# Revit family: TYCO-FPP-Zettler-QRM850 Quad relay output module
name_source: partatom
category: Electrical Fixtures
revit_build: Autodesk Revit 2014 (Build: 20130308_1515(x64)
units: mm (PartAtom-declared; Revit-internal decimal feet)

## types (1)
- TYCO-FPP-Zettler-QRM850 Quad relay output module
    Alarm current = 5.9 mA
    Approvals = EN54-17, EN54-18 and
EN54-13
    Battery Requirements = Standby current
1.1 mA
    Description = The Quad Relay Output Module connects directly to the
MZX Digital loop and provides four change over relay
outputs or four High Voltage Relay (HVR) outputs.
    Keynote = Four change over relay outputs each individually
programmable for a wide range of applications
    Length = 103 mm
    Manufacturer = Tyco
    Model = Zettler -555.800.073
    Operating Humidity = Up to 95 %
    Operating Temperature = -25 to +70 oC
    PCB = PCB
    RS = RS
    RSS = res
    ST = ST12
    Storage Temparature = 40 to +80 oC
    Type Comments = It is
loop powered and therefore does not need a power
supply, however it can monitor the presence of a local
24Vdc or 48Vdc power supply.
    URL = https://tycosafetyproducts-anz.com
    Width = 134 mm
    Wire Size = Min. 0.5 mm2, max. 2.5 mm2

## geometry (parser evidence)
native form markers: Sweep x1
no freeform markers — native parametric forms only
